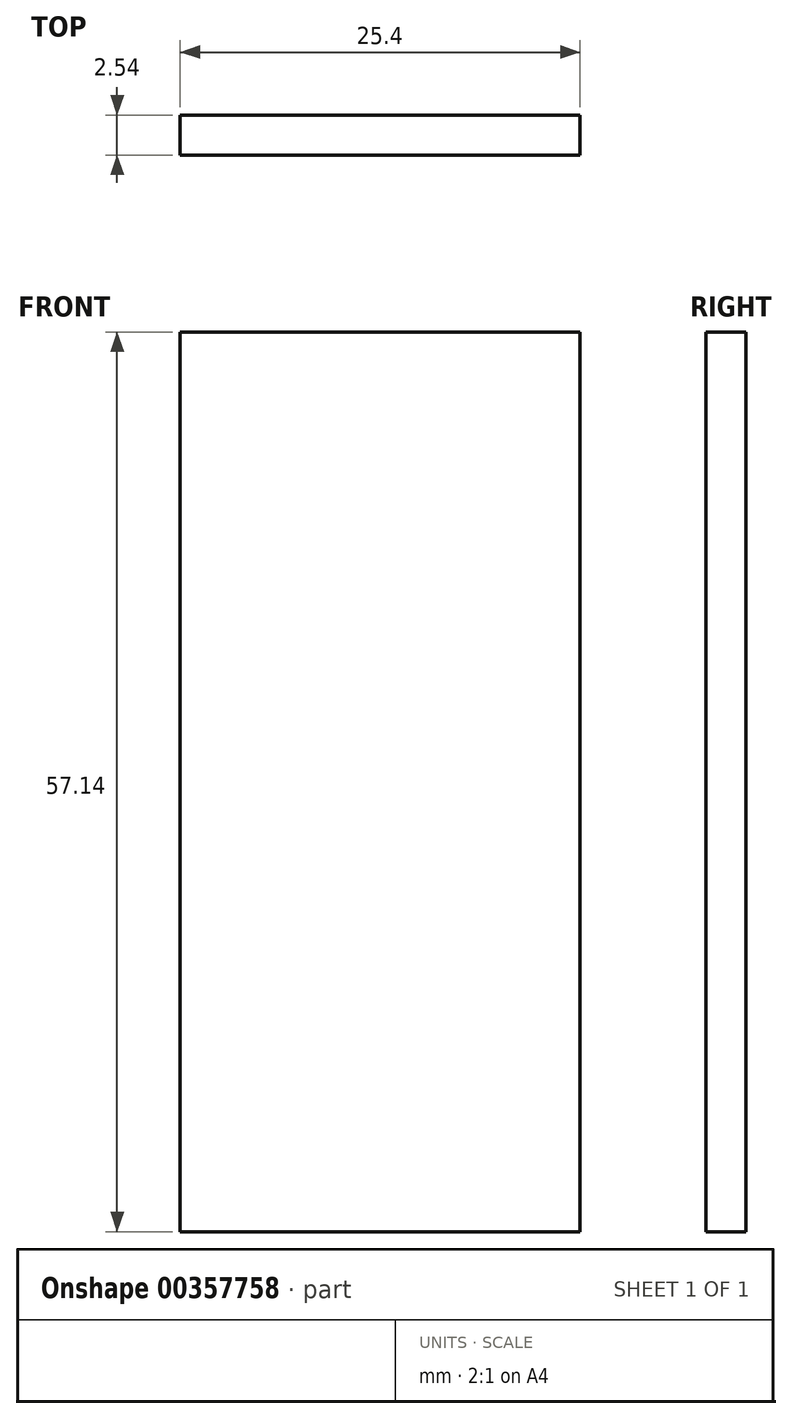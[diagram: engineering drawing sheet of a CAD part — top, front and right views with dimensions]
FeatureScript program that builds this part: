
annotation { "Feature Type Name" : "Feature", "Feature Type Description" : "" }
export const myFeature = defineFeature(function(context is Context, id is Id, definition is map)
    precondition{}
    {
        {
            var Q0;
            Q0=qCreatedBy(makeId("Front.planeOp"),FACE);
            var sketch = newSketch(context, id + "F0", { "sketchPlane" : qUnion([Q0])});
            skLineSegment(sketch, "E0.bottom", {"start": v(12.7, -28.58) * mm, "end": v(-12.7, -28.58) * mm});
            skLineSegment(sketch, "E0.top", {"start": v(12.7, 28.58) * mm, "end": v(-12.7, 28.58) * mm});
            skLineSegment(sketch, "E0.left", {"start": v(12.7, -28.58) * mm, "end": v(12.7, 28.58) * mm});
            skLineSegment(sketch, "E0.right", {"start": v(-12.7, -28.58) * mm, "end": v(-12.7, 28.58) * mm});
            skPoint(sketch, "E0.middle", {"position": v(0, 0) * mm});
            skSolve(sketch);
        }
        {
            var Q0;
            Q0=makeQuery(id+"F0.imprint","IMPRINT",FACE,{"disambiguationData":[TD([[makeQuery(id+"F0.imprint","IMPRINT",EDGE,{"derivedFrom":sQuery(id+"F0.wireOp",EDGE,"E0.bottom")}),-1.0]])]});
            extrude(context, id + "F1", {"entities" : qUnion([Q0]), "depth" : 2.54 * mm});
        }
    });
